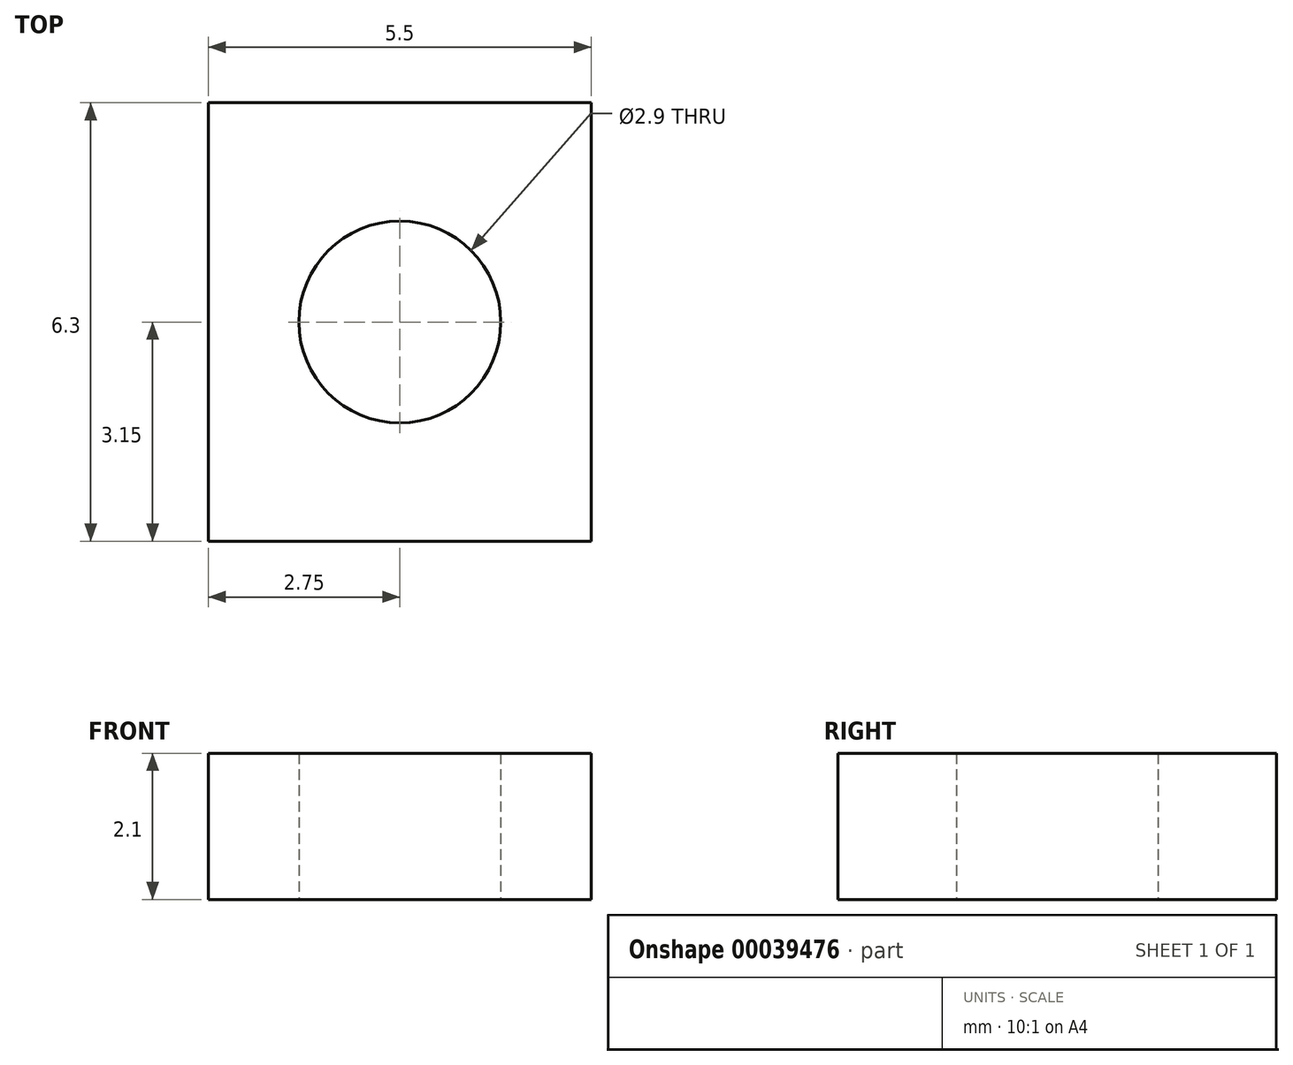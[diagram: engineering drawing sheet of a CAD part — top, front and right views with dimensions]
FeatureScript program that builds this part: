
annotation { "Feature Type Name" : "Feature", "Feature Type Description" : "" }
export const myFeature = defineFeature(function(context is Context, id is Id, definition is map)
    precondition{}
    {
        {
            var Q0;
            Q0=qCreatedBy(makeId("Top.planeOp"),FACE);
            var sketch = newSketch(context, id + "F0", { "sketchPlane" : qUnion([Q0])});
            skLineSegment(sketch, "E0.rect.bottom", {"start": v(2.75, -3.15) * mm, "end": v(-2.75, -3.15) * mm});
            skLineSegment(sketch, "E0.rect.top", {"start": v(2.75, 3.15) * mm, "end": v(-2.75, 3.15) * mm});
            skLineSegment(sketch, "E0.rect.left", {"start": v(2.75, -3.15) * mm, "end": v(2.75, 3.15) * mm});
            skLineSegment(sketch, "E0.rect.right", {"start": v(-2.75, -3.15) * mm, "end": v(-2.75, 3.15) * mm});
            skPoint(sketch, "E0.rect.middle", {"position": v(0, 0) * mm});
            skCircle(sketch, "E1", {"center": v(0, 0) * mm, "radius": 1.45 * mm});
            skSolve(sketch);
        }
        {
            var Q0;
            Q0=makeQuery(id+"F0.imprint","IMPRINT",FACE,{"disambiguationData":[TD([[makeQuery(id+"F0.imprint","IMPRINT",EDGE,{"derivedFrom":sQuery(id+"F0.wireOp",EDGE,"E0.rect.bottom")}),-1.0]])]});
            extrude(context, id + "F1", {"entities" : qUnion([Q0]), "depth" : 2.1 * mm});
        }
    });
